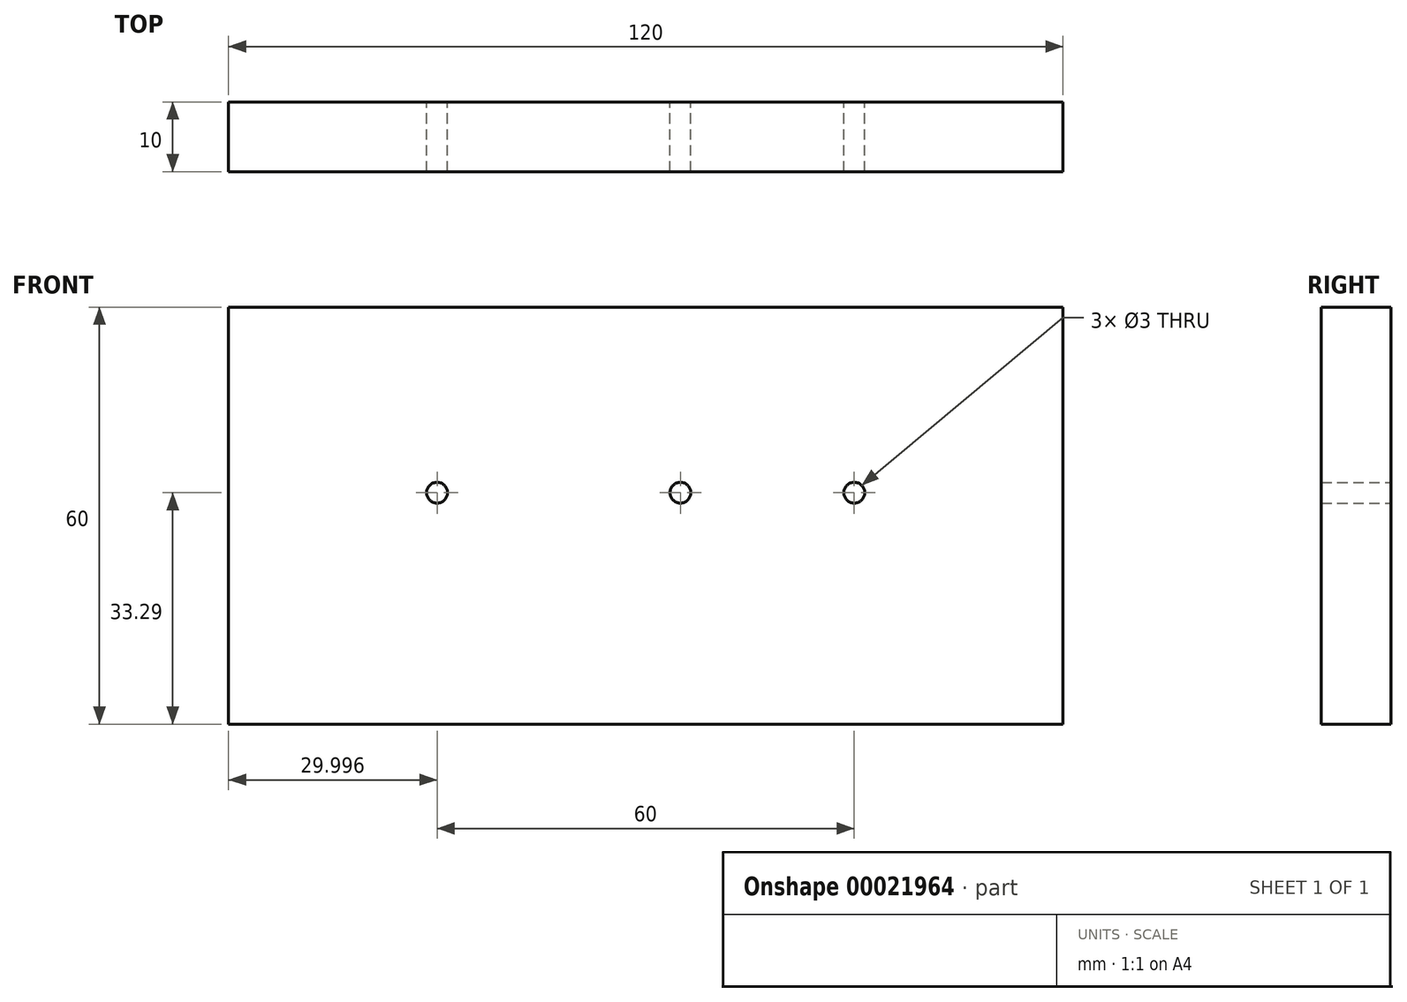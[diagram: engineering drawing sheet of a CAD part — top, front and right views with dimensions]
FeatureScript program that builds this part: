
annotation { "Feature Type Name" : "Feature", "Feature Type Description" : "" }
export const myFeature = defineFeature(function(context is Context, id is Id, definition is map)
    precondition{}
    {
        {
            var Q0;
            Q0=qCreatedBy(makeId("Front.planeOp"),FACE);
            var sketch = newSketch(context, id + "F0", { "sketchPlane" : qUnion([Q0])});
            skLineSegment(sketch, "E0.bottom", {"start": v(-58.97, 26.71) * mm, "end": v(61.03, 26.71) * mm});
            skLineSegment(sketch, "E0.top", {"start": v(-58.97, -33.29) * mm, "end": v(61.03, -33.29) * mm});
            skLineSegment(sketch, "E0.left", {"start": v(-58.97, 26.71) * mm, "end": v(-58.97, -33.29) * mm});
            skLineSegment(sketch, "E0.right", {"start": v(61.03, 26.71) * mm, "end": v(61.03, -33.29) * mm});
            skCircle(sketch, "E1", {"center": v(-28.97, 0) * mm, "radius": 1.5 * mm});
            skCircle(sketch, "E2", {"center": v(6.03, 0) * mm, "radius": 1.5 * mm});
            skCircle(sketch, "E3", {"center": v(31.03, 0) * mm, "radius": 1.5 * mm});
            skLineSegment(sketch, "E4", {"start": v(-41.8, 26.71) * mm, "end": v(-41.8, -33.29) * mm});
            skSolve(sketch);
        }
        {
            var Q0;
            {var subQ1=sQuery(id+"F0.wireOp",EDGE,"E0.left");Q0=makeQuery(id+"F0.imprint","IMPRINT",FACE,{"disambiguationData":[TD([[makeQuery(id+"F0.imprint","IMPRINT",EDGE,{"derivedFrom":subQ1}),1.0]])]});}
            var Q1;
            {var subQ1=sQuery(id+"F0.wireOp",EDGE,"E0.right");Q1=makeQuery(id+"F0.imprint","IMPRINT",FACE,{"disambiguationData":[TD([[makeQuery(id+"F0.imprint","IMPRINT",EDGE,{"derivedFrom":subQ1}),-1.0]])]});}
            extrude(context, id + "F1", {"entities" : qUnion([Q0, Q1]), "depth" : 10 * mm});
        }
    });
